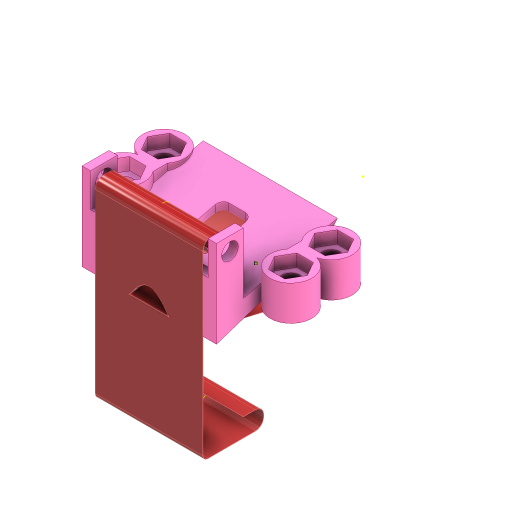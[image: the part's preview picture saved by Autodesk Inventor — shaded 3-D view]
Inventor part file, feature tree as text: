
AUTODESK INVENTOR PART (.ipt)
format: ipt  version: 2024 (Build 280153000, 153)  size: 1,850,880 bytes
history: native  units: mm
features: sketch x24, extrude x19, projected_geometry x11, split x10, other x10, loft x6, boolean_combine x5, plane x4, fillet x2, sweep x2, thicken_offset x2
ambient origin geometry x8: Origin, YZ Plane, XZ Plane, XY Plane, X Axis, Y Axis, Z Axis, Center Point
bodies: Solid1 (feature_tree), Solid2 (feature_tree), Solid19 (feature_tree), Solid20 (feature_tree), Solid21 (feature_tree), Solid22 (feature_tree), Solid23 (feature_tree), Solid3 (feature_tree), Solid4 (feature_tree), Solid5 (feature_tree), Solid6 (feature_tree), Solid7 (feature_tree), Solid8 (feature_tree), Solid9 (feature_tree), Solid10 (feature_tree), Solid11 (feature_tree), Solid12 (feature_tree), Solid13 (feature_tree), Solid14 (feature_tree), Solid15 (feature_tree), Solid16 (feature_tree), Solid17 (feature_tree), Solid18 (feature_tree)
feature tree (95):
  extrude  "Extrusion1"  Depth=3.0mm TaperAngle=0.0deg
  extrude  "Extrusion2"  Depth=3.0mm TaperAngle=0.0deg
  extrude  "Extrusion3"  Depth=40.0mm
  plane  "Work Plane2"
  sketch  "Sketch4"  dims[d4=29.0mm d5=3.0mm d6=0.0mm]
  loft  "Loft1"
  loft  "Loft2"
  loft  "Loft3"
  loft  "Loft4"
  boolean_combine  "Combine1"
  loft  "Loft5"
  fillet  "Fillet1"  [1 undecoded]
  fillet  "Fillet2"  [1 undecoded]
  plane  "Work Plane3"
  extrude  "Extrusion5"  TaperAngle=0.0deg  [1 undecoded]
  extrude  "Extrusion6"  TaperAngle=0.0deg  [1 undecoded]
  extrude  "Extrusion7"  Depth=40.0mm
  extrude  "Extrusion8"  TaperAngle=0.0deg  [1 undecoded]
  extrude  "Extrusion9"  Depth=2.0mm
  extrude  "Extrusion10"  Depth=38.0mm
  extrude  "Extrusion11"  Depth=3.0mm TaperAngle=0.0deg
  extrude  "Extrusion12"  Depth=3.0mm TaperAngle=0.0deg
  extrude  "Extrusion13"  Depth=12.5mm TaperAngle=0.0deg
  extrude  "Extrusion14"  Depth=3.7mm TaperAngle=0.0deg
  extrude  "Extrusion15"  Depth=8.5mm
  split  "Split1"
  split  "Split2"
  split  "Split3"
  split  "Split4"
  split  "Split5"
  split  "Split6"
  split  "Split7"
  boolean_combine  "Combine2"
  split  "Split8"
  boolean_combine  "Combine3"
  boolean_combine  "Combine4"
  extrude  "Extrusion16"  Depth=8.5mm
  extrude  "Extrusion17"  Depth=2.7mm TaperAngle=0.0deg
  sketch  "Sketch36"  dims[d47=15.0mm d48=3.0mm d49=0.0mm]
  sweep  "Sweep1"
  split  "Split9"
  loft  "Loft6"
  thicken_offset  "Thicken1"
  extrude  "Extrusion18"  Depth=10.0mm TaperAngle=0.0deg
  sweep  "Sweep2"
  split  "Split10"
  thicken_offset  "Thicken2"
  boolean_combine  "Combine5"
  plane  "Work Plane4"
  extrude  "Extrusion19"  Depth=10.0mm
  other  "Work Point1"
  other  "Work Point2"
  other  "Work Point3"
  extrude  "Extrusion20"  Depth=10.0mm
  sketch  "Sketch1"  dims[d0=3.0mm d1=0.0mm d2=9.5mm d3=0.0mm]
  plane  "Work Plane1"
  other  "2D Equation Curve1"
  other  "Edges1"
  other  "Edges2"
  other  "Edges3"
  other  "Edges4"
  sketch  "Sketch7"  dims[d7=12.0mm d8=36.0mm d9=40.0mm]
  sketch  "Sketch10"  dims[d10=9.0mm d11=10.0mm]
  sketch  "Sketch12"  dims[d12=3.0mm d13=-6.0mm d14=6.0mm]
  sketch  "Sketch13"  dims[d15=40.0mm d16=26.0mm]
  sketch  "Sketch16"  dims[d17=20.0mm d18=20.0mm]
  projected_geometry  "Projected Loop1"
  sketch  "Sketch18"  dims[d19=0.0mm d20=90.0deg d21=0.0mm d22=90.0deg d23=0.0mm d24=90.0deg d25=0.0mm d26=90.0deg]
  sketch  "Sketch19"  dims[d27=0.0mm d28=90.0deg d29=0.0mm d30=90.0deg]
  projected_geometry  "Projected Loop2"
  projected_geometry  "Projected Loop3"
  projected_geometry  "Projected Loop4"
  projected_geometry  "Projected Loop5"
  sketch  "Sketch23"  dims[d31=0.0mm d32=90.0deg d33=0.0mm d34=90.0deg]
  sketch  "Sketch24"  dims[d35=26.0mm d36=40.0mm]
  sketch  "Sketch28"  dims[d37=4.0mm d38=0.0mm d39=90.0deg]
  sketch  "Sketch29"  dims[d40=0.0mm d41=90.0deg d42=2.0mm]
  sketch  "Sketch35"  dims[d43=1.5mm d46=38.0mm]
  projected_geometry  "Projected Loop11"
  sketch  "3D Sketch2"
  other  "Srf1"
  sketch  "Sketch38"  dims[d50=15.0mm d51=3.0mm d52=0.0mm]
  projected_geometry  "Projected Loop12"
  sketch  "Sketch42"  dims[d53=11.0mm d54=12.5mm d55=0.0mm]
  projected_geometry  "Projected Loop19"
  projected_geometry  "Projected Loop20"
  sketch  "Sketch43"  dims[d56=11.0mm d57=3.7mm d58=0.0mm]
  sketch  "Sketch46"  dims[d59=20.0mm d60=0.0mm d61=8.5mm]
  projected_geometry  "Projected Loop21"
  sketch  "3D Sketch3"
  sketch  "Sketch47"  dims[d62=8.5mm d63=8.5mm]
  projected_geometry  "Projected Loop22"
  sketch  "Sketch49"  dims[d64=8.5mm d65=2.7mm d66=0.0mm]
  sketch  "Sketch50"  dims[d67=40.0mm d68=10.0mm d69=2.7mm d70=0.0mm d71=2.5mm d72=0.0mm d73=2.5mm d74=0.0mm d75=9.0mm d76=2.0mm d77=0.0mm d78=0.0mm d79=7.0mm d80=5.5mm d81=8.5mm d82=8.5mm d83=2.5mm d84=0.0mm d85=2.5mm d86=0.0mm d87=0.5mm d88=0.0mm d89=0.0mm d91=10.0mm d92=10.0mm d93=0.1mm d94=0.0mm d95=16.0mm d96=2.5mm d97=4.0mm d98=2.5mm d99=2.5mm d100=5.0mm d101=5.0mm d102=2.5mm d103=2.5mm d104=2.5mm d105=2.5mm d106=0.0mm d107=0.0mm d108=2.5mm d109=2.5mm d110=0.0mm d111=90.0deg d112=0.0mm d113=90.0deg d114=0.1mm d115=0.1mm d116=0.1mm d117=0.0mm d118=15.0mm d119=3.0mm d120=1.6mm d121=1.5mm d122=16.5mm d125=5.5mm d126=2.5mm d127=2.5mm d128=0.0mm d129=0.0mm d130=0.1mm d131=0.1mm d132=58.25mm d133=6.0mm d134=16.0mm d135=0.0mm d136=12.0mm d137=12.0mm d138=12.0mm d139=12.0mm d140=10.0mm d141=0.0mm]
  other  "Unwrap1"
note: 5 required parameter values undecoded (feature->parameter linkage not recoverable at this tier; creation-order binding heuristic only, values carry confidence <= 0.55)
